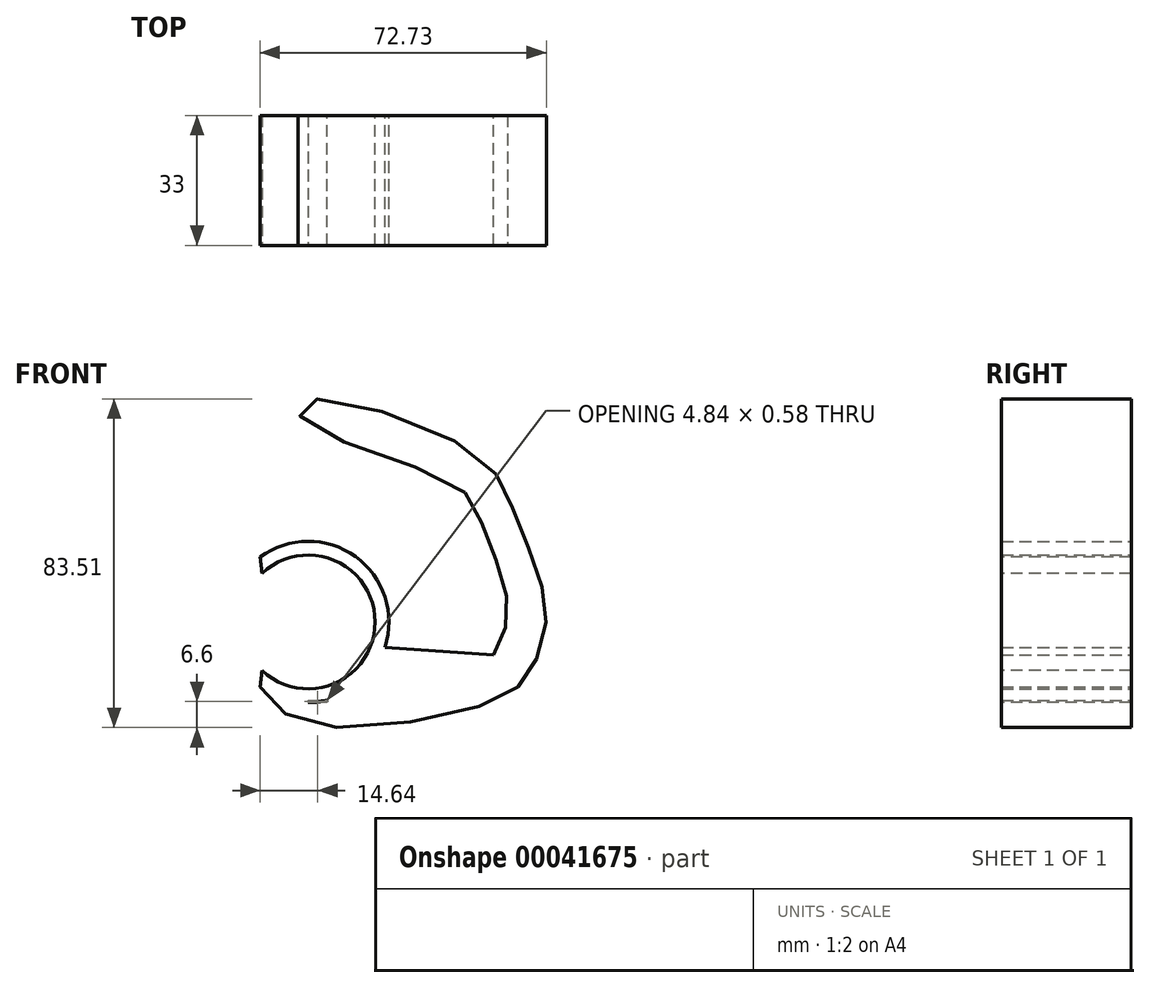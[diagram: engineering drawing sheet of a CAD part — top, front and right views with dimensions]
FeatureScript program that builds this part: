
annotation { "Feature Type Name" : "Feature", "Feature Type Description" : "" }
export const myFeature = defineFeature(function(context is Context, id is Id, definition is map)
    precondition{}
    {
        {
            var Q0;
            Q0=qCreatedBy(makeId("Front.planeOp"),FACE);
            var sketch = newSketch(context, id + "F0", { "sketchPlane" : qUnion([Q0])});
            skCircle(sketch, "E0", {"center": v(0, 0) * mm, "radius": 20.5 * mm});
            skCircle(sketch, "E1", {"center": v(0, 0) * mm, "radius": 17 * mm});
            skFitSpline(sketch, "E2", {"points": [v(0, -20.5) * mm, v(41.57, -11.54) * mm, v(47.13, -8.4) * mm, v(50.46, 0) * mm, v(49.54, 10.13) * mm, v(44.16, 24.94) * mm, v(36.57, 35.31) * mm, v(-1.4, 51.43) * mm, v(-0.47, 56.24) * mm, v(41.57, 43.28) * mm, v(51.57, 29.76) * mm, v(58.05, 13.09) * mm, v(60.46, 0) * mm, v(56.39, -12.65) * mm, v(45.83, -20.62) * mm, v(0, -25.8) * mm, v(-12.22, -16.46) * mm], "startDerivative": vector(492.2, 49.85) * mm, "endDerivative": vector(-136.07, 189.5) * mm});
            skLineSegment(sketch, "E3", {"start": v(19.47, -6.4) * mm, "end": v(47.13, -8.4) * mm});
            skSolve(sketch);
        }
        {
            var Q0;
            Q0=makeQuery(id+"F0.imprint","IMPRINT",FACE,{"disambiguationData":[TD([[makeQuery(id+"F0.imprint","IMPRINT",EDGE,{"derivedFrom":sQuery(id+"F0.wireOp",EDGE,"E1")}),-1.0]])]});
            var Q1;
            {var subQ0=sQuery(id+"F0.wireOp",EDGE,"E3");Q1=makeQuery(id+"F0.imprint","IMPRINT",FACE,{"disambiguationData":[TD([[makeQuery(id+"F0.imprint","IMPRINT",EDGE,{"derivedFrom":subQ0}),-1.0]])]});}
            var Q2;
            {var subQ0=sQuery(id+"F0.wireOp",EDGE,"E2");var subQ2=sQuery(id+"F0.wireOp",EDGE,"E0");var subQ5=makeQuery(id+"F0.imprint","INTERSECT",VERTEX,{"disambiguationData":[OD(0.0)],"derivedFrom":[subQ2,subQ0]});Q2=makeQuery(id+"F0.imprint","IMPRINT",FACE,{"disambiguationData":[TD([[makeQuery(id+"F0.imprint","IMPRINT",EDGE,{"disambiguationData":[TD([[subQ5,1.0]])],"derivedFrom":subQ2}),-1.0]])]});}
            extrude(context, id + "F1", {"entities" : qUnion([Q0, Q1, Q2]), "depth" : 33 * mm});
        }
        {
            var Q0;
            Q0=makeQuery(id+"F1.opExtrude","CAP_FACE",FACE,{"disambiguationData":[OSD([sQuery(id+"F0.wireOp",EDGE,"E0"),sQuery(id+"F0.wireOp",EDGE,"56f00c67-c97a-42e0-b06e-e0fecf1b1397"),sQuery(id+"F0.wireOp",EDGE,"69cb8554-0612-4449-bbc3-75f5126ca61a"),sQuery(id+"F0.wireOp",EDGE,"c11cc40f-4b2b-4dc3-a6b5-edcea72b161c"),sQuery(id+"F0.wireOp",EDGE,"0bdd9e2b-e035-456b-b674-e893ffb524f9"),sQuery(id+"F0.wireOp",EDGE,"bf6cbe0e-5ab5-4528-992f-e6734639df4b"),sQuery(id+"F0.wireOp",EDGE,"efb6c8bf-9522-461e-818a-b1d44ccd6082"),sQuery(id+"F0.wireOp",EDGE,"30318dfa-d482-4cdf-900e-23ef0aa96013"),sQuery(id+"F0.wireOp",EDGE,"E1"),sQuery(id+"F0.wireOp",EDGE,"18f40852-e071-4c55-b064-dcf17eec00f6"),sQuery(id+"F0.wireOp",EDGE,"1591c549-fc7c-4fd2-a5af-2d705f43a49d"),sQuery(id+"F0.wireOp",EDGE,"8783f71a-b3dd-4929-b214-a3c2f23ebe95")])],"isStart":false});
            var sketch = newSketch(context, id + "F2", { "sketchPlane" : qUnion([Q0])});
            skArc(sketch, "E4", {"start": v(-12.22, -16.46) * mm, "mid": v(-11.12, 0) * mm, "end": v(-12.22, 16.46) * mm});
            skSolve(sketch);
        }
        {
            var Q0;
            {var subQ5=sQuery(id+"F2.wireOp",EDGE,"E4");var subQ8=makeQuery(id+"F1.opExtrude","CAP_EDGE",EDGE,{"disambiguationData":[OSD([sQuery(id+"F0.wireOp",EDGE,"E1")])],"isStart":false});var subQ10=makeQuery(id+"F2.imprint","INTERSECT",VERTEX,{"disambiguationData":[OD(0.0)],"derivedFrom":[subQ8,subQ5]});Q0=makeQuery(id+"F2.imprint","IMPRINT",FACE,{"disambiguationData":[TD([[makeQuery(id+"F2.imprint","IMPRINT",EDGE,{"disambiguationData":[TD([[subQ10,1.0]])],"derivedFrom":subQ8}),-1.0]])]});}
            extrude(context, id + "F3", {"entities" : qUnion([Q0]), "operationType" : NewBodyOperationType.REMOVE, "oppositeDirection" : true, "depth" : 34 * mm});
        }
    });
